# Revit family: PTT, 1812,2112,2412
name_source: partatom
category: Windows
revit_build: Autodesk Revit LT 2016 (Build: 20150220_1215(x64)
units: mm (PartAtom-declared; Revit-internal decimal feet)

## family parameters
Always vertical = Yes
Cut with Voids When Loaded = No
Host = Wall
OmniClass Number = 23.30.20.00
OmniClass Title = Windows
Room Calculation Point = No
Shared = No

## types (3) — shared parameters
Aluminium anodized = Aluminium
Bottom fixed glass width = 6 mm  [stored 0.019685 ft]
Centre fixed glass width = 6 mm  [stored 0.019685 ft]
Centre vert mullion = 910 mm
Default Sill Height = 914 mm
Description = Anodized Aluminium
Glazing = Glass
Height = 1210 mm  [stored 3.96982 ft]
Manufacturer = Robmeg
Plaster = 5 mm  [stored 0.0164042 ft]
Rough Height = 1219 mm
Top hung = Yes
Top mullion = 600 mm
URL = http://www.robmeg.co.za
Wall Closure = By host

## per-type parameters (varying)
| type | Model | Width |
| PTT Type- 1812 | PTT 1812 | 1810 mm  [stored 5.93832 ft] |
| PTT Type- 2112 | PTT 2112 | 2110 mm  [stored 6.92257 ft] |
| PTT Type- 2412 | PTT 2412 | 2410 mm  [stored 7.90682 ft] |

note: [stored X ft] marks values corroborated as IEEE doubles in the binary element streams (Revit-internal decimal feet)

## geometry (parser evidence)
native form markers: Sweep x3
no freeform markers — native parametric forms only
